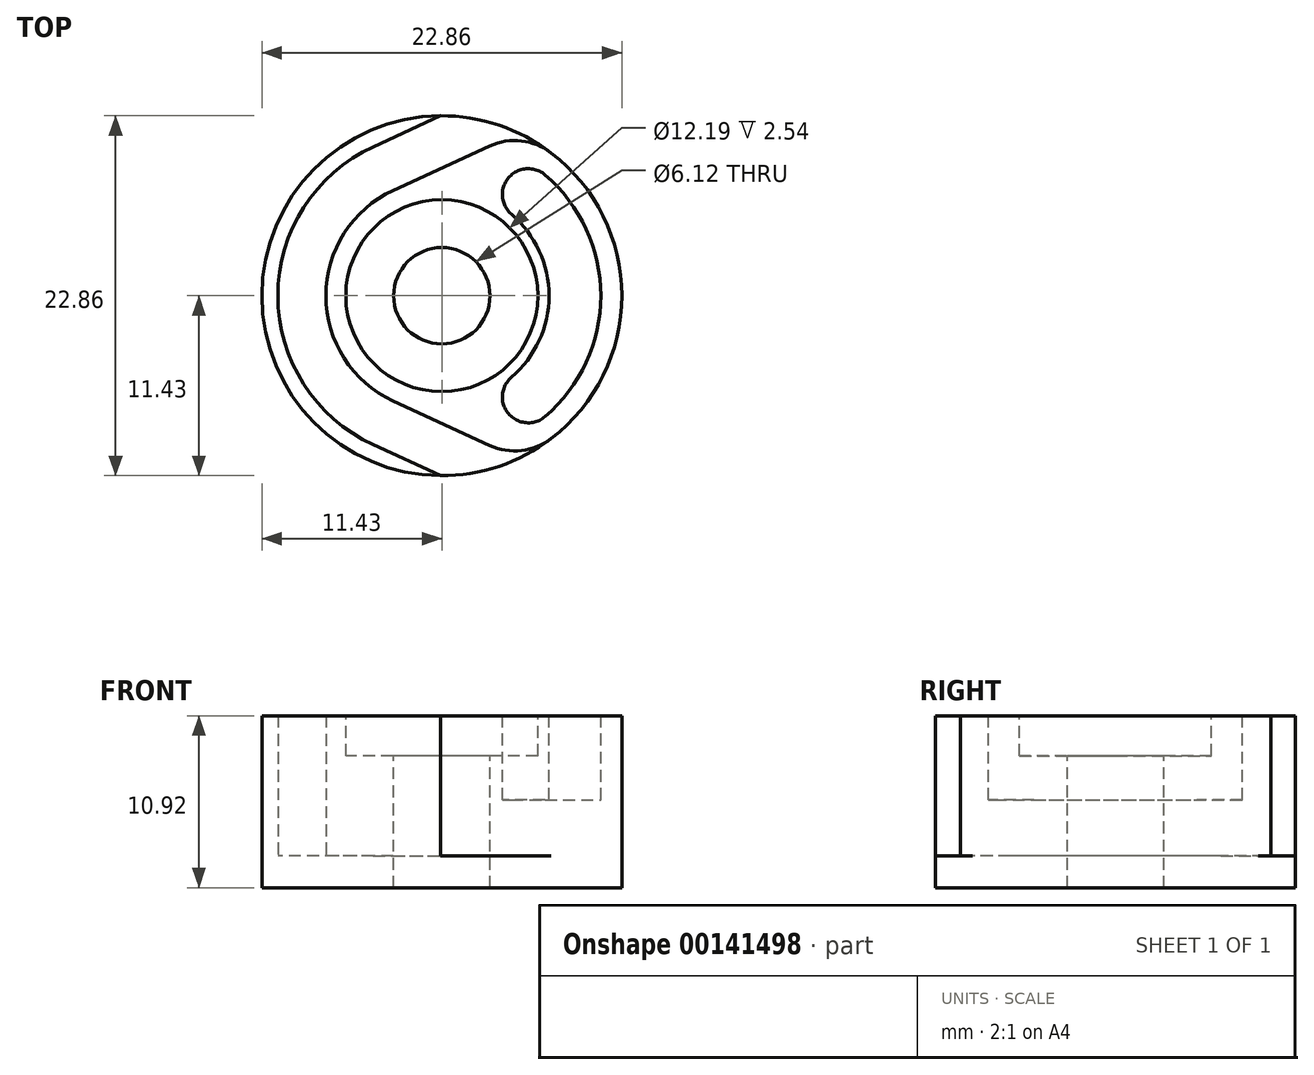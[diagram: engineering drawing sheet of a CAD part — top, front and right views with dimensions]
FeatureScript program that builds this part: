
annotation { "Feature Type Name" : "Feature", "Feature Type Description" : "" }
export const myFeature = defineFeature(function(context is Context, id is Id, definition is map)
    precondition{}
    {
        {
            var Q0;
            Q0=qCreatedBy(makeId("Top.planeOp"),FACE);
            var sketch = newSketch(context, id + "F0", { "sketchPlane" : qUnion([Q0])});
            skCircle(sketch, "E0", {"center": v(0, 0) * mm, "radius": 11.43 * mm});
            skSolve(sketch);
        }
        {
            var Q0;
            Q0=makeQuery(id+"F0.imprint","IMPRINT",FACE,{"disambiguationData":[TD([[makeQuery(id+"F0.imprint","IMPRINT",EDGE,{"derivedFrom":sQuery(id+"F0.wireOp",EDGE,"E0")}),1.0]])]});
            extrude(context, id + "F1", {"entities" : qUnion([Q0]), "oppositeDirection" : true, "depth" : 2.03 * mm});
        }
        {
            var Q0;
            Q0=qCreatedBy(makeId("Top.planeOp"),FACE);
            var sketch = newSketch(context, id + "F2", { "sketchPlane" : qUnion([Q0])});
            skArc(sketch, "E1", {"start": v(-3.08, 6.69) * mm, "mid": v(-7.37, 0) * mm, "end": v(-3.08, -6.69) * mm});
            skArc(sketch, "E2", {"start": v(-0.08, 11.43) * mm, "mid": v(-11.43, 0) * mm, "end": v(-0.08, -11.43) * mm});
            skArc(sketch, "E3", {"start": v(-4.36, 9.46) * mm, "mid": v(-10.41, 0) * mm, "end": v(-4.36, -9.46) * mm});
            skLineSegment(sketch, "E4", {"start": v(-3.08, 6.69) * mm, "end": v(3.04, 9.51) * mm});
            skLineSegment(sketch, "E5", {"start": v(-3.08, -6.69) * mm, "end": v(3.04, -9.51) * mm});
            skLineSegment(sketch, "E6", {"start": v(-4.36, 9.46) * mm, "end": v(-0.08, 11.43) * mm});
            skLineSegment(sketch, "E7", {"start": v(-4.36, -9.46) * mm, "end": v(-0.08, -11.43) * mm});
            skArc(sketch, "E8.trimOffspring", {"start": v(3.6, -9.77) * mm, "mid": v(3.64, -9.76) * mm, "end": v(3.68, -9.74) * mm});
            skArc(sketch, "E9.trimOffspring", {"start": v(6.95, -9.08) * mm, "mid": v(11.43, 0) * mm, "end": v(6.95, 9.08) * mm});
            skArc(sketch, "E10", {"start": v(6.95, 9.08) * mm, "mid": v(5.05, 9.84) * mm, "end": v(3.04, 9.51) * mm});
            skArc(sketch, "E11", {"start": v(3.04, -9.51) * mm, "mid": v(5.05, -9.84) * mm, "end": v(6.95, -9.08) * mm});
            skArc(sketch, "E12.trimOffspring", {"start": v(3.68, 9.74) * mm, "mid": v(3.64, 9.76) * mm, "end": v(3.6, 9.77) * mm});
            skSolve(sketch);
        }
        {
            var Q0;
            Q0=makeQuery(id+"F2.imprint","IMPRINT",FACE,{"disambiguationData":[TD([[makeQuery(id+"F2.imprint","IMPRINT",EDGE,{"derivedFrom":sQuery(id+"F2.wireOp",EDGE,"E2")}),1.0]])]});
            var Q1;
            Q1=makeQuery(id+"F2.imprint","IMPRINT",FACE,{"disambiguationData":[TD([[makeQuery(id+"F2.imprint","IMPRINT",EDGE,{"derivedFrom":sQuery(id+"F2.wireOp",EDGE,"E1")}),1.0]])]});
            extrude(context, id + "F3", {"entities" : qUnion([Q0, Q1]), "operationType" : NewBodyOperationType.ADD, "depth" : 8.9 * mm});
        }
        {
            var Q0;
            Q0=makeQuery(id+"F3.opExtrude","CAP_FACE",FACE,{"disambiguationData":[OSD([sQuery(id+"F2.wireOp",EDGE,"E1"),sQuery(id+"F2.wireOp",EDGE,"E4"),sQuery(id+"F2.wireOp",EDGE,"E5"),sQuery(id+"F2.wireOp",EDGE,"E9.trimOffspring"),sQuery(id+"F2.wireOp",EDGE,"E10"),sQuery(id+"F2.wireOp",EDGE,"E11")])],"isStart":false});
            var sketch = newSketch(context, id + "F4", { "sketchPlane" : qUnion([Q0])});
            skCircle(sketch, "E13", {"center": v(0, 0) * mm, "radius": 6.1 * mm});
            skSolve(sketch);
        }
        {
            var Q0;
            Q0=makeQuery(id+"F4.imprint","IMPRINT",FACE,{"disambiguationData":[TD([[makeQuery(id+"F4.imprint","IMPRINT",EDGE,{"derivedFrom":sQuery(id+"F4.wireOp",EDGE,"E13")}),1.0]])]});
            extrude(context, id + "F5", {"entities" : qUnion([Q0]), "operationType" : NewBodyOperationType.REMOVE, "oppositeDirection" : true, "depth" : 2.54 * mm});
        }
        {
            var Q0;
            Q0=makeQuery(id+"F3.opExtrude","CAP_FACE",FACE,{"disambiguationData":[OSD([sQuery(id+"F2.wireOp",EDGE,"E1"),sQuery(id+"F2.wireOp",EDGE,"E4"),sQuery(id+"F2.wireOp",EDGE,"E5"),sQuery(id+"F2.wireOp",EDGE,"E9.trimOffspring"),sQuery(id+"F2.wireOp",EDGE,"E10"),sQuery(id+"F2.wireOp",EDGE,"E11")])],"isStart":false});
            var sketch = newSketch(context, id + "F6", { "sketchPlane" : qUnion([Q0])});
            skArc(sketch, "E14", {"start": v(6.56, -7.68) * mm, "mid": v(10.1, 0) * mm, "end": v(6.56, 7.68) * mm});
            skArc(sketch, "E15", {"start": v(4.42, -5.18) * mm, "mid": v(6.8, 0) * mm, "end": v(4.42, 5.18) * mm});
            skArc(sketch, "E16", {"start": v(6.56, 7.68) * mm, "mid": v(4.24, 7.5) * mm, "end": v(4.42, 5.18) * mm});
            skArc(sketch, "E17", {"start": v(4.42, -5.18) * mm, "mid": v(4.24, -7.5) * mm, "end": v(6.56, -7.68) * mm});
            skLineSegment(sketch, "E18", {"start": v(0, 0) * mm, "end": v(5.49, 6.43) * mm, "construction": true});
            skLineSegment(sketch, "E19", {"start": v(0, 0) * mm, "end": v(5.49, -6.43) * mm, "construction": true});
            skSolve(sketch);
        }
        {
            var Q0;
            Q0=makeQuery(id+"F6.imprint","IMPRINT",FACE,{"disambiguationData":[TD([[makeQuery(id+"F6.imprint","IMPRINT",EDGE,{"derivedFrom":sQuery(id+"F6.wireOp",EDGE,"E14")}),1.0]])]});
            extrude(context, id + "F7", {"entities" : qUnion([Q0]), "operationType" : NewBodyOperationType.REMOVE, "oppositeDirection" : true, "depth" : 5.33 * mm});
        }
        {
            var Q0;
            Q0=makeQuery(id+"F3.opExtrude","CAP_FACE",FACE,{"disambiguationData":[OSD([sQuery(id+"F2.wireOp",EDGE,"E1"),sQuery(id+"F2.wireOp",EDGE,"E4"),sQuery(id+"F2.wireOp",EDGE,"E5"),sQuery(id+"F2.wireOp",EDGE,"E9.trimOffspring"),sQuery(id+"F2.wireOp",EDGE,"E10"),sQuery(id+"F2.wireOp",EDGE,"E11")])],"isStart":false});
            var sketch = newSketch(context, id + "F8", { "sketchPlane" : qUnion([Q0])});
            skCircle(sketch, "E20", {"center": v(0, 0) * mm, "radius": 3.06 * mm});
            skSolve(sketch);
        }
        {
            var Q0;
            Q0 = qSketchRegion(id + "F8", true);
            extrude(context, id + "F9", {"entities" : qUnion([Q0]), "operationType" : NewBodyOperationType.REMOVE, "endBound" : BoundingType.THROUGH_ALL, "oppositeDirection" : true, "depth" : 25.4 * mm});
        }
    });
